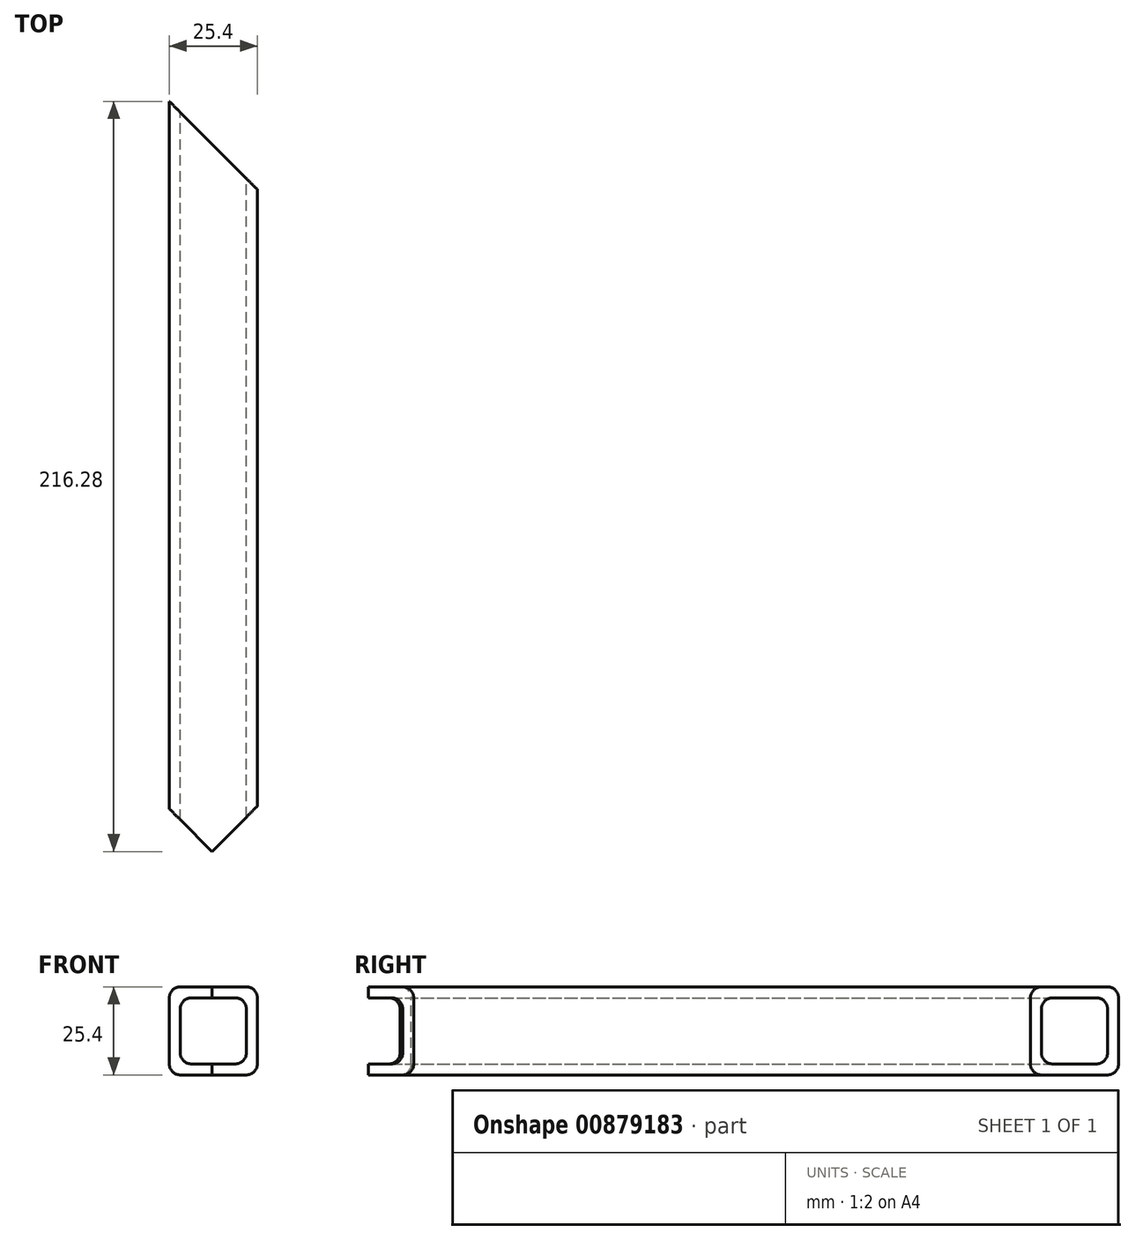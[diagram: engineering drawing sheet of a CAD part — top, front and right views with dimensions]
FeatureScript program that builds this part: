
annotation { "Feature Type Name" : "Feature", "Feature Type Description" : "" }
export const myFeature = defineFeature(function(context is Context, id is Id, definition is map)
    precondition{}
    {
        {
            var Q0;
            Q0=qCreatedBy(makeId("Front.planeOp"),FACE);
            var sketch = newSketch(context, id + "F0", { "sketchPlane" : qUnion([Q0])});
            skLineSegment(sketch, "E0.bottom", {"start": v(9.9, -12.8) * mm, "end": v(-9.15, -12.8) * mm});
            skLineSegment(sketch, "E0.top", {"start": v(9.9, 12.6) * mm, "end": v(-9.15, 12.6) * mm});
            skLineSegment(sketch, "E0.left", {"start": v(13.08, -9.62) * mm, "end": v(13.08, 9.43) * mm});
            skLineSegment(sketch, "E0.right", {"start": v(-12.32, -9.62) * mm, "end": v(-12.32, 9.43) * mm});
            skLineSegment(sketch, "E1.bottom", {"start": v(6.73, -9.62) * mm, "end": v(-5.97, -9.62) * mm});
            skLineSegment(sketch, "E1.top", {"start": v(6.73, 9.43) * mm, "end": v(-5.97, 9.43) * mm});
            skLineSegment(sketch, "E1.left", {"start": v(9.9, -6.44) * mm, "end": v(9.9, 6.26) * mm});
            skLineSegment(sketch, "E1.right", {"start": v(-9.15, -6.44) * mm, "end": v(-9.15, 6.26) * mm});
            skPoint(sketch, "E2.visualSharp", {"position": v(9.9, 9.43) * mm});
            skArc(sketch, "E2.filletArc", {"start": v(9.9, 6.26) * mm, "mid": v(8.97, 8.5) * mm, "end": v(6.73, 9.43) * mm});
            skPoint(sketch, "E3.visualSharp", {"position": v(-9.15, 9.43) * mm});
            skArc(sketch, "E3.filletArc", {"start": v(-5.97, 9.43) * mm, "mid": v(-8.22, 8.5) * mm, "end": v(-9.15, 6.26) * mm});
            skPoint(sketch, "E4.visualSharp", {"position": v(-9.15, -9.62) * mm});
            skArc(sketch, "E4.filletArc", {"start": v(-9.15, -6.44) * mm, "mid": v(-8.22, -8.69) * mm, "end": v(-5.97, -9.62) * mm});
            skPoint(sketch, "E5.visualSharp", {"position": v(9.9, -9.62) * mm});
            skArc(sketch, "E5.filletArc", {"start": v(6.73, -9.62) * mm, "mid": v(8.97, -8.69) * mm, "end": v(9.9, -6.44) * mm});
            skPoint(sketch, "E6.visualSharp", {"position": v(13.08, 12.6) * mm});
            skArc(sketch, "E6.filletArc", {"start": v(13.08, 9.43) * mm, "mid": v(12.15, 11.68) * mm, "end": v(9.9, 12.6) * mm});
            skPoint(sketch, "E7.visualSharp", {"position": v(-12.32, 12.6) * mm});
            skArc(sketch, "E7.filletArc", {"start": v(-9.15, 12.6) * mm, "mid": v(-11.4, 11.68) * mm, "end": v(-12.32, 9.43) * mm});
            skPoint(sketch, "E8.visualSharp", {"position": v(-12.32, -12.8) * mm});
            skArc(sketch, "E8.filletArc", {"start": v(-12.32, -9.62) * mm, "mid": v(-11.4, -11.86) * mm, "end": v(-9.15, -12.8) * mm});
            skPoint(sketch, "E9.visualSharp", {"position": v(13.08, -12.8) * mm});
            skArc(sketch, "E9.filletArc", {"start": v(9.9, -12.8) * mm, "mid": v(12.15, -11.86) * mm, "end": v(13.08, -9.62) * mm});
            skSolve(sketch);
        }
        {
            var Q0;
            Q0=qSketchRegion(id+"F0",true);
            extrude(context, id + "F1", {"entities" : qUnion([Q0]), "depth" : 228.6 * mm, "offsetDistance" : 25.4 * mm});
        }
        {
            var Q0;
            Q0=makeQuery(id+"F1.opExtrude","SWEPT_FACE",FACE,{"disambiguationData":[OSD([sQuery(id+"F0.wireOp",EDGE,"E0.top")])]});
            var sketch = newSketch(context, id + "F2", { "sketchPlane" : qUnion([Q0])});
            skLineSegment(sketch, "E10", {"start": v(-12.32, 0) * mm, "end": v(13.08, -25.4) * mm});
            skLineSegment(sketch, "E11", {"start": v(13.08, -25.4) * mm, "end": v(13.08, 0) * mm});
            skLineSegment(sketch, "E12", {"start": v(13.08, 0) * mm, "end": v(-12.32, 0) * mm});
            skSolve(sketch);
        }
        {
            var Q0;
            Q0=qSketchRegion(id+"F2",true);
            extrude(context, id + "F3", {"entities" : qUnion([Q0]), "operationType" : NewBodyOperationType.REMOVE, "oppositeDirection" : true, "depth" : 25.4 * mm, "offsetDistance" : 25.4 * mm});
        }
        {
            var Q0;
            Q0=makeQuery(id+"F1.opExtrude","SWEPT_FACE",FACE,{"disambiguationData":[OSD([sQuery(id+"F0.wireOp",EDGE,"E0.bottom")])]});
            var sketch = newSketch(context, id + "F4", { "sketchPlane" : qUnion([Q0])});
            skLineSegment(sketch, "E13", {"start": v(-12.32, 228.6) * mm, "end": v(13.08, 203.2) * mm});
            skLineSegment(sketch, "E14", {"start": v(13.08, 203.2) * mm, "end": v(13.08, 228.6) * mm});
            skLineSegment(sketch, "E15", {"start": v(13.08, 228.6) * mm, "end": v(-12.32, 228.6) * mm});
            skSolve(sketch);
        }
        {
            var Q0;
            Q0=qSketchRegion(id+"F4",true);
            extrude(context, id + "F5", {"entities" : qUnion([Q0]), "operationType" : NewBodyOperationType.REMOVE, "oppositeDirection" : true, "depth" : 25.4 * mm, "offsetDistance" : 25.4 * mm});
        }
        {
            var Q0;
            Q0=makeQuery(id+"F1.opExtrude","SWEPT_FACE",FACE,{"disambiguationData":[OSD([sQuery(id+"F0.wireOp",EDGE,"E0.bottom")])]});
            var sketch = newSketch(context, id + "F6", { "sketchPlane" : qUnion([Q0])});
            skLineSegment(sketch, "E16", {"start": v(0, 216.28) * mm, "end": v(-40.98, 175.3) * mm});
            skLineSegment(sketch, "E17", {"start": v(-40.98, 175.3) * mm, "end": v(-40.98, 257.26) * mm});
            skLineSegment(sketch, "E18", {"start": v(-40.98, 257.26) * mm, "end": v(0, 216.28) * mm});
            skSolve(sketch);
        }
        {
            var Q0;
            Q0=qSketchRegion(id+"F6",true);
            extrude(context, id + "F7", {"entities" : qUnion([Q0]), "operationType" : NewBodyOperationType.REMOVE, "oppositeDirection" : true, "depth" : 25.4 * mm, "offsetDistance" : 25.4 * mm});
        }
    });
